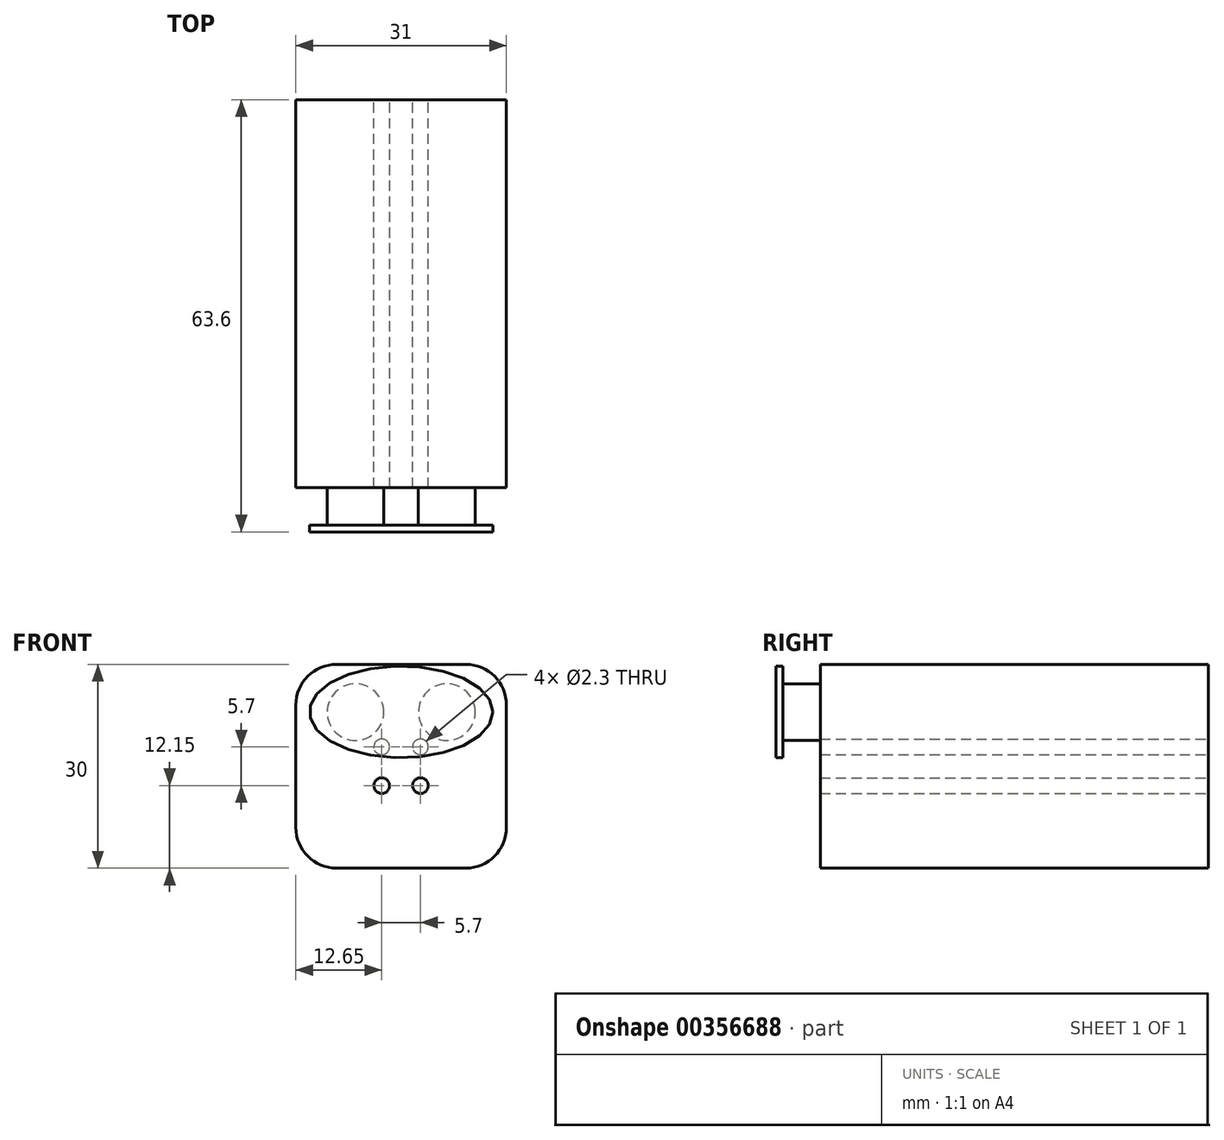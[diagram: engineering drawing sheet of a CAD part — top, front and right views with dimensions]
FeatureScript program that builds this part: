
annotation { "Feature Type Name" : "Feature", "Feature Type Description" : "" }
export const myFeature = defineFeature(function(context is Context, id is Id, definition is map)
    precondition{}
    {
        {
            var Q0;
            Q0=qCreatedBy(makeId("Front.planeOp"),FACE);
            var sketch = newSketch(context, id + "F0", { "sketchPlane" : qUnion([Q0])});
            skLineSegment(sketch, "E0.bottom", {"start": v(15.5, -15) * mm, "end": v(-15.5, -15) * mm});
            skLineSegment(sketch, "E0.top", {"start": v(15.5, 15) * mm, "end": v(-15.5, 15) * mm});
            skLineSegment(sketch, "E0.left", {"start": v(15.5, -15) * mm, "end": v(15.5, 15) * mm});
            skLineSegment(sketch, "E0.right", {"start": v(-15.5, -15) * mm, "end": v(-15.5, 15) * mm});
            skPoint(sketch, "E0.middle", {"position": v(0, 0) * mm});
            skSolve(sketch);
        }
        {
            var Q0;
            Q0=qSketchRegion(id+"F0",true);
            extrude(context, id + "F1", {"entities" : qUnion([Q0]), "endBound" : BoundingType.SYMMETRIC, "depth" : 57.1 * mm});
        }
        {
            var Q0;
            Q0=makeQuery(id+"F1.opExtrude","CAP_FACE",FACE,{"disambiguationData":[OSD([sQuery(id+"F0.wireOp",EDGE,"E0.bottom"),sQuery(id+"F0.wireOp",EDGE,"E0.top"),sQuery(id+"F0.wireOp",EDGE,"E0.left"),sQuery(id+"F0.wireOp",EDGE,"E0.right")])],"isStart":true});
            var sketch = newSketch(context, id + "F2", { "sketchPlane" : qUnion([Q0])});
            skCircle(sketch, "E1", {"center": v(-2.85, 2.85) * mm, "radius": 1.15 * mm});
            skCircle(sketch, "E2", {"center": v(-2.85, -2.85) * mm, "radius": 1.15 * mm});
            skCircle(sketch, "E3", {"center": v(2.85, 2.85) * mm, "radius": 1.15 * mm});
            skCircle(sketch, "E4", {"center": v(2.85, -2.85) * mm, "radius": 1.15 * mm});
            skLineSegment(sketch, "E5", {"start": v(-2.85, 2.85) * mm, "end": v(0, 2.85) * mm, "construction": true});
            skLineSegment(sketch, "E6", {"start": v(0, 2.85) * mm, "end": v(2.85, 2.85) * mm, "construction": true});
            skLineSegment(sketch, "E7", {"start": v(-2.85, 2.85) * mm, "end": v(-2.85, 0) * mm, "construction": true});
            skLineSegment(sketch, "E8", {"start": v(-2.85, 0) * mm, "end": v(-2.85, -2.85) * mm, "construction": true});
            skLineSegment(sketch, "E9", {"start": v(-2.85, -2.85) * mm, "end": v(0, -2.85) * mm, "construction": true});
            skLineSegment(sketch, "E10", {"start": v(0, -2.85) * mm, "end": v(2.85, -2.85) * mm, "construction": true});
            skLineSegment(sketch, "E11", {"start": v(2.85, 2.85) * mm, "end": v(2.85, 0) * mm, "construction": true});
            skLineSegment(sketch, "E12", {"start": v(2.85, 0) * mm, "end": v(2.85, -2.85) * mm, "construction": true});
            skSolve(sketch);
        }
        {
            var Q0;
            Q0=makeQuery(id+"F2.imprint","IMPRINT",FACE,{"disambiguationData":[TD([[makeQuery(id+"F2.imprint","IMPRINT",EDGE,{"derivedFrom":sQuery(id+"F2.wireOp",EDGE,"E1")}),1.0]])]});
            var Q1;
            Q1=makeQuery(id+"F2.imprint","IMPRINT",FACE,{"disambiguationData":[TD([[makeQuery(id+"F2.imprint","IMPRINT",EDGE,{"derivedFrom":sQuery(id+"F2.wireOp",EDGE,"E3")}),1.0]])]});
            var Q2;
            Q2=makeQuery(id+"F2.imprint","IMPRINT",FACE,{"disambiguationData":[TD([[makeQuery(id+"F2.imprint","IMPRINT",EDGE,{"derivedFrom":sQuery(id+"F2.wireOp",EDGE,"E2")}),1.0]])]});
            var Q3;
            Q3=makeQuery(id+"F2.imprint","IMPRINT",FACE,{"disambiguationData":[TD([[makeQuery(id+"F2.imprint","IMPRINT",EDGE,{"derivedFrom":sQuery(id+"F2.wireOp",EDGE,"E4")}),1.0]])]});
            extrude(context, id + "F3", {"entities" : qUnion([Q0, Q1, Q2, Q3]), "operationType" : NewBodyOperationType.REMOVE, "endBound" : BoundingType.THROUGH_ALL, "oppositeDirection" : true, "depth" : 100 * mm});
        }
        {
            var Q0;
            Q0=makeQuery(id+"F1.opExtrude","CAP_FACE",FACE,{"disambiguationData":[OSD([sQuery(id+"F0.wireOp",EDGE,"E0.bottom"),sQuery(id+"F0.wireOp",EDGE,"E0.top"),sQuery(id+"F0.wireOp",EDGE,"E0.left"),sQuery(id+"F0.wireOp",EDGE,"E0.right")])],"isStart":false});
            var sketch = newSketch(context, id + "F4", { "sketchPlane" : qUnion([Q0])});
            skCircle(sketch, "E13", {"center": v(6.72, 7.96) * mm, "radius": 4.17 * mm});
            skCircle(sketch, "E14", {"center": v(-6.73, 7.96) * mm, "radius": 4.17 * mm});
            skSolve(sketch);
        }
        {
            var Q0;
            Q0=qSketchRegion(id+"F4",true);
            extrude(context, id + "F5", {"entities" : qUnion([Q0]), "operationType" : NewBodyOperationType.ADD, "depth" : 5.5 * mm});
        }
        {
            var Q0;
            Q0=makeQuery(id+"F5.opExtrude","CAP_FACE",FACE,{"disambiguationData":[OSD([sQuery(id+"F4.wireOp",EDGE,"E14")])],"isStart":false});
            var sketch = newSketch(context, id + "F6", { "sketchPlane" : qUnion([Q0])});
            skEllipse(sketch, "E15", {"center": v(0, 8) * mm, "majorRadius": 13.5 * mm, "minorRadius": 6.75 * mm, "majorAxis": v(1, 0)});
            skSolve(sketch);
        }
        {
            var Q0;
            Q0=qSketchRegion(id+"F6",true);
            extrude(context, id + "F7", {"entities" : qUnion([Q0]), "operationType" : NewBodyOperationType.ADD, "depth" : 1 * mm});
        }
        {
            var Q0;
            Q0=makeQuery(id+"F1.opExtrude","SWEPT_EDGE",EDGE,{"disambiguationData":[OSD([sQuery(id+"F0.wireOp",EDGE,"E0.top"),sQuery(id+"F0.wireOp",EDGE,"E0.right")])]});
            var Q1;
            Q1=makeQuery(id+"F1.opExtrude","SWEPT_EDGE",EDGE,{"disambiguationData":[OSD([sQuery(id+"F0.wireOp",EDGE,"E0.top"),sQuery(id+"F0.wireOp",EDGE,"E0.left")])]});
            var Q2;
            Q2=makeQuery(id+"F1.opExtrude","SWEPT_EDGE",EDGE,{"disambiguationData":[OSD([sQuery(id+"F0.wireOp",EDGE,"E0.bottom"),sQuery(id+"F0.wireOp",EDGE,"E0.right")])]});
            var Q3;
            Q3=makeQuery(id+"F1.opExtrude","SWEPT_EDGE",EDGE,{"disambiguationData":[OSD([sQuery(id+"F0.wireOp",EDGE,"E0.bottom"),sQuery(id+"F0.wireOp",EDGE,"E0.left")])]});
            fillet(context, id + "F8", {"entities" : qUnion([Q0, Q1, Q2, Q3]), "radius" : 6 * mm, "tangentPropagation" : true, "allowEdgeOverflow" : false});
        }
    });
